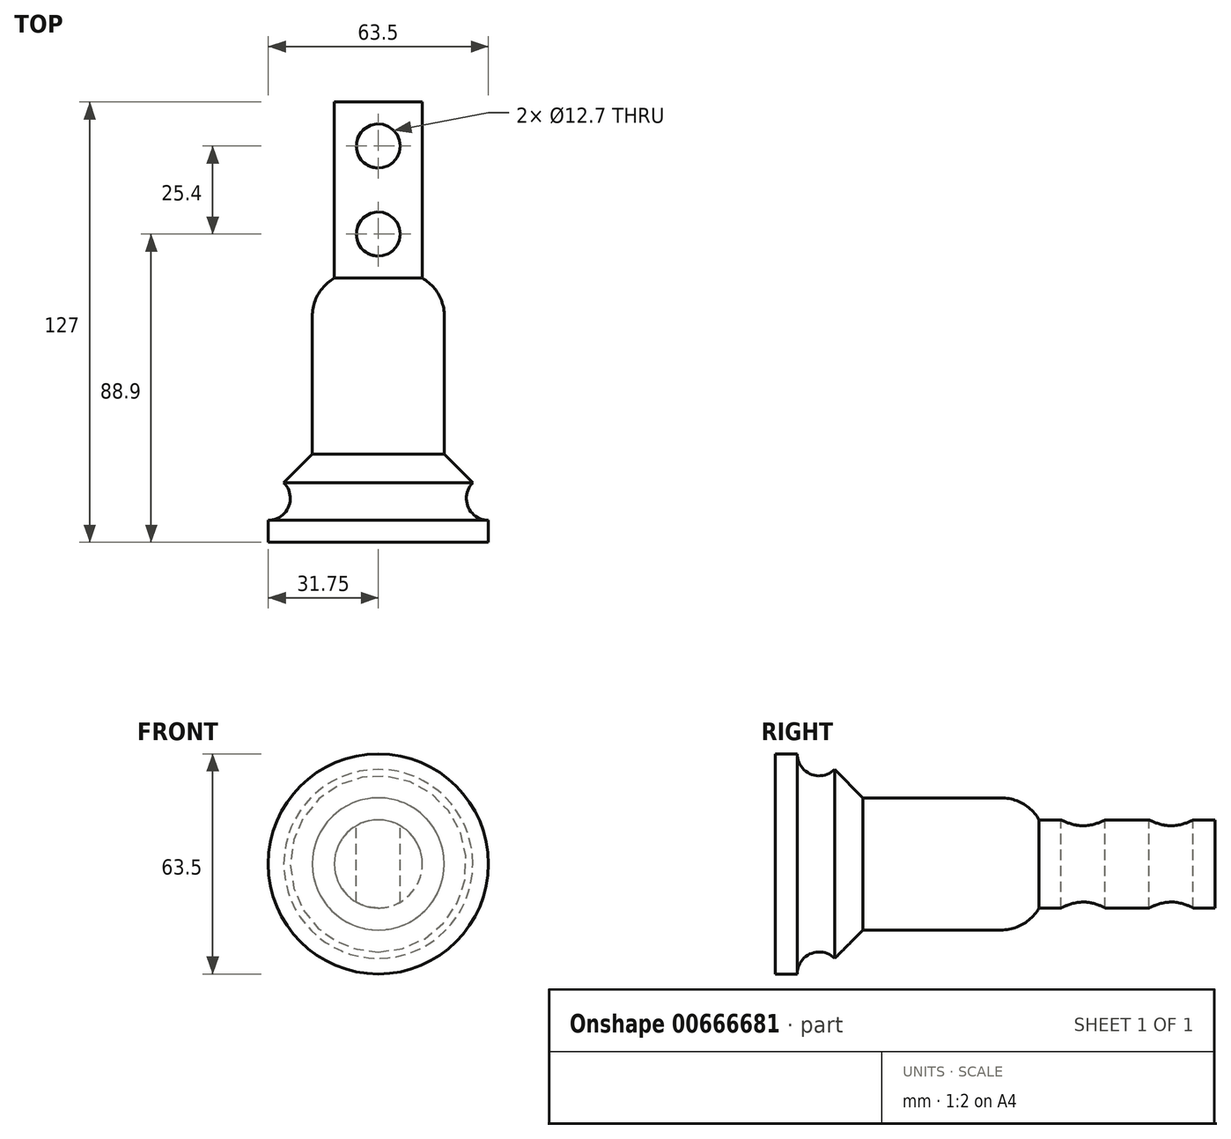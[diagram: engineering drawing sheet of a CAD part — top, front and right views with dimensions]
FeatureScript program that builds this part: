
annotation { "Feature Type Name" : "Feature", "Feature Type Description" : "" }
export const myFeature = defineFeature(function(context is Context, id is Id, definition is map)
    precondition{}
    {
        {
            var Q0;
            Q0=qCreatedBy(makeId("Front.planeOp"),FACE);
            var sketch = newSketch(context, id + "F0", { "sketchPlane" : qUnion([Q0])});
            skCircle(sketch, "E0", {"center": v(0, 0) * mm, "radius": 12.7 * mm});
            skSolve(sketch);
        }
        {
            var Q0;
            Q0 = qSketchRegion(id + "F0", false);
            extrude(context, id + "F1", {"entities" : qUnion([Q0]), "depth" : 50.8 * mm});
        }
        {
            var Q0;
            Q0=makeQuery(id+"F1.opExtrude","CAP_FACE",FACE,{"disambiguationData":[OSD([sQuery(id+"F0.wireOp",EDGE,"E0")])],"isStart":false});
            var sketch = newSketch(context, id + "F2", { "sketchPlane" : qUnion([Q0])});
            skCircle(sketch, "E0", {"center": v(0, 0) * mm, "radius": 19.05 * mm});
            skSolve(sketch);
        }
        {
            var Q0;
            Q0 = qSketchRegion(id + "F2", false);
            extrude(context, id + "F3", {"entities" : qUnion([Q0]), "operationType" : NewBodyOperationType.ADD, "depth" : 50.8 * mm});
        }
        {
            var Q0;
            Q0=makeQuery(id+"F3.opExtrude","CAP_FACE",FACE,{"disambiguationData":[OSD([sQuery(id+"F2.wireOp",EDGE,"E0")])],"isStart":false});
            var sketch = newSketch(context, id + "F4", { "sketchPlane" : qUnion([Q0])});
            skCircle(sketch, "E0", {"center": v(0, 0) * mm, "radius": 31.75 * mm});
            skSolve(sketch);
        }
        {
            var Q0;
            Q0 = qSketchRegion(id + "F4", false);
            extrude(context, id + "F5", {"entities" : qUnion([Q0]), "operationType" : NewBodyOperationType.ADD, "depth" : 25.4 * mm});
        }
        {
            var Q0;
            Q0=qCreatedBy(makeId("Top.planeOp"),FACE);
            var sketch = newSketch(context, id + "F6", { "sketchPlane" : qUnion([Q0])});
            skCircle(sketch, "E1", {"center": v(0, -38.1) * mm, "radius": 6.35 * mm});
            skSolve(sketch);
        }
        {
            var Q0;
            Q0 = qSketchRegion(id + "F6", false);
            extrude(context, id + "F7", {"entities" : qUnion([Q0]), "operationType" : NewBodyOperationType.REMOVE, "endBound" : BoundingType.UP_TO_NEXT, "oppositeDirection" : true, "hasSecondDirection" : true, "secondDirectionBound" : SecondDirectionBoundingType.UP_TO_NEXT, "secondDirectionOppositeDirection" : false});
        }
        {
            var Q0;
            Q0=qCreatedBy(makeId("Top.planeOp"),FACE);
            var sketch = newSketch(context, id + "F8", { "sketchPlane" : qUnion([Q0])});
            skCircle(sketch, "E1", {"center": v(0, -12.7) * mm, "radius": 6.35 * mm});
            skSolve(sketch);
        }
        {
            var Q0;
            Q0 = qSketchRegion(id + "F8", false);
            extrude(context, id + "F9", {"entities" : qUnion([Q0]), "operationType" : NewBodyOperationType.REMOVE, "endBound" : BoundingType.UP_TO_NEXT, "oppositeDirection" : true, "hasSecondDirection" : true, "secondDirectionBound" : SecondDirectionBoundingType.UP_TO_NEXT, "secondDirectionOppositeDirection" : false});
        }
        {
            var Q0;
            Q0=makeQuery(id+"F3.opExtrude","CAP_EDGE",EDGE,{"disambiguationData":[OSD([sQuery(id+"F2.wireOp",EDGE,"E0")])],"isStart":true});
            fillet(context, id + "F10", {"entities" : qUnion([Q0]), "radius" : 12.7 * mm, "allowEdgeOverflow" : false});
        }
        {
            var Q0;
            Q0=makeQuery(id+"F5.opExtrude","CAP_FACE",FACE,{"disambiguationData":[OSD([sQuery(id+"F4.wireOp",EDGE,"E0")])],"isStart":false});
            cPlane(context, id + "F11", {"entities" : qUnion([Q0]), "cplaneType" : CPlaneType.OFFSET, "offset" : 12.7 * mm, "oppositeDirection" : true, "width" : 152.4 * mm, "height" : 152.4 * mm});
        }
        {
            var Q0;
            Q0=qCreatedBy(id+"F11.planeOp",FACE);
            var sketch = newSketch(context, id + "F12", { "sketchPlane" : qUnion([Q0])});
            skCircle(sketch, "E0", {"center": v(0, 0) * mm, "radius": 31.75 * mm});
            skSolve(sketch);
        }
        {
            var Q0;
            Q0=qCreatedBy(makeId("Right.planeOp"),FACE);
            var sketch = newSketch(context, id + "F13", { "sketchPlane" : qUnion([Q0])});
            skCircle(sketch, "E2", {"center": v(-114.3, 31.75) * mm, "radius": 6.35 * mm});
            skSolve(sketch);
        }
        {
            var Q0;
            Q0=makeQuery(id+"F13.imprint","IMPRINT",FACE,{"disambiguationData":[TD([[makeQuery(id+"F13.imprint","IMPRINT",EDGE,{"derivedFrom":sQuery(id+"F13.wireOp",EDGE,"E2")}),1.0]])]});
            var Q1;
            Q1=sQuery(id+"F12.wireOp",EDGE,"E0");
            sweep(context, id + "F14", {"operationType" : NewBodyOperationType.REMOVE, "profiles" : qUnion([Q0]), "path" : qUnion([Q1])});
        }
        {
            var Q0;
            Q0=makeQuery(id+"F5.opExtrude","CAP_EDGE",EDGE,{"disambiguationData":[OSD([sQuery(id+"F4.wireOp",EDGE,"E0")])],"isStart":true});
            chamfer(context, id + "F15", {"entities" : qUnion([Q0]), "width" : 12.7 * mm});
        }
    });
